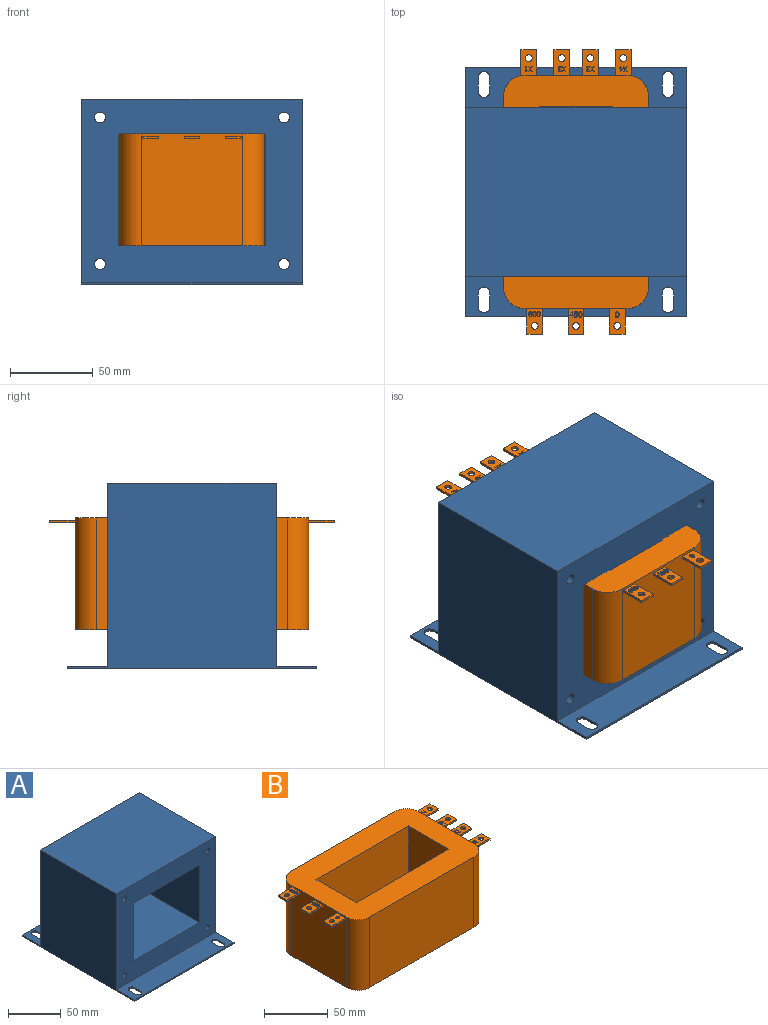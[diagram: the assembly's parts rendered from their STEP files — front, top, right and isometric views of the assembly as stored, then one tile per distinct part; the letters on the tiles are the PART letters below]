
ASSEMBLY  parts=2 mates=1
PART A: 34 faces, bbox 133.5x151x112.5 mm
  f0: plane 133.5x111mm, normal (0,-1,0), area 8744.3mm2, adj f2,f4,f22,f25,f26,f27,f28,f29
  f1: plane 133.5x111mm, normal (0,1,0), area 8744.3mm2, adj f4,f22,f23,f25,f26,f27,f28,f29
  f2: plane 133.5x24.35mm, normal (0,0,1), area 3052.5mm2, adj f0,f3,f4,f9,f10,f11,f12,f13
  f3: plane 133.5x1.5mm, normal (0,-1,0), area 200.2mm2, adj f2,f4,f22,f24
  f4: plane 151x112.5mm, normal (1,0,0), area 11581.8mm2, adj f0,f1,f2,f3,f5,f23,f24,f25
  f5: plane 133.5x1.5mm, normal (0,1,0), area 200.2mm2, adj f4,f22,f23,f24
  f6: cylinder r=3.54mm len=7.09mm, axis (0,0,-1), area 16.7mm2, adj f7,f18,f23,f24
  f7: plane 8.41x1.5mm, normal (-1,0,0), area 12.6mm2, adj f6,f8,f23,f24
  f8: cylinder r=3.54mm len=7.09mm, axis (0,0,-1), area 16.7mm2, adj f7,f18,f23,f24
  f9: plane 8.41x1.5mm, normal (-1,0,0), area 12.6mm2, adj f2,f10,f19,f24
  f10: cylinder r=3.54mm len=7.09mm, axis (0,0,-1), area 16.7mm2, adj f2,f9,f11,f24
  f11: plane 8.41x1.5mm, normal (1,0,0), area 12.6mm2, adj f2,f10,f19,f24
  f12: plane 8.41x1.5mm, normal (-1,0,0), area 12.6mm2, adj f2,f13,f20,f24
  f13: cylinder r=3.54mm len=7.09mm, axis (0,0,-1), area 16.7mm2, adj f2,f12,f14,f24
  f14: plane 8.41x1.5mm, normal (1,0,0), area 12.6mm2, adj f2,f13,f20,f24
  f15: plane 8.41x1.5mm, normal (1,0,0), area 12.6mm2, adj f16,f21,f23,f24
  f16: cylinder r=3.54mm len=7.09mm, axis (0,0,-1), area 16.7mm2, adj f15,f17,f23,f24
  f17: plane 8.41x1.5mm, normal (-1,0,0), area 12.6mm2, adj f16,f21,f23,f24
  f18: plane 8.41x1.5mm, normal (1,0,0), area 12.6mm2, adj f6,f8,f23,f24
  f19: cylinder r=3.54mm len=7.09mm, axis (0,0,-1), area 16.7mm2, adj f2,f9,f11,f24
  f20: cylinder r=3.54mm len=7.09mm, axis (0,0,-1), area 16.7mm2, adj f2,f12,f14,f24
  f21: cylinder r=3.54mm len=7.09mm, axis (0,0,-1), area 16.7mm2, adj f15,f17,f23,f24
  f22: plane 151x112.5mm, normal (-1,0,0), area 11581.8mm2, adj f0,f1,f2,f3,f5,f23,f24,f25
  f23: plane 133.5x24.35mm, normal (0,0,1), area 3052.5mm2, adj f1,f4,f5,f6,f7,f8,f15,f16
  f24: plane 151x133.5mm, normal (0,0,-1), area 19762.1mm2, adj f3,f4,f5,f6,f7,f8,f9,f10
  f25: plane 133.5x102.3mm, normal (0,0,1), area 13657mm2, adj f0,f1,f4,f22
  f26: plane 102.3x88.75mm, normal (0,0,1), area 9079.1mm2, adj f0,f1,f27,f29
  f27: plane 102.3x66.9mm, normal (-1,0,0), area 6843.9mm2, adj f0,f1,f26,f28
  f28: plane 102.3x88.75mm, normal (0,0,-1), area 9079.1mm2, adj f0,f1,f27,f29
  f29: plane 102.3x66.9mm, normal (1,0,0), area 6843.9mm2, adj f0,f1,f26,f28
  f30: cylinder r=3.3mm len=102.3mm, axis (0,-1,0), area 2121.1mm2, adj f0,f1
  f31: cylinder r=3.3mm len=102.3mm, axis (0,-1,0), area 2121.1mm2, adj f0,f1
  f32: cylinder r=3.3mm len=102.3mm, axis (0,-1,0), area 2121.1mm2, adj f0,f1
  f33: cylinder r=3.3mm len=102.3mm, axis (0,-1,0), area 2121.1mm2, adj f0,f1
PART B: 341 faces, bbox 172.3x87.8x67.6 mm
  f0: plane 15.5x9.5mm, normal (0,0,1), area 117.8mm2, adj f13,f36,f37,f38,f49,f271,f272,f273
  f1: plane 15.5x9.5mm, normal (0,0,1), area 127.1mm2, adj f13,f39,f41,f42,f48,f256,f257,f258
  f2: plane 15.5x9.5mm, normal (0,0,1), area 118.8mm2, adj f13,f43,f45,f46,f47,f196,f197,f198
  f3: plane 15.3x9.5mm, normal (0,0,1), area 127.8mm2, adj f9,f17,f19,f20,f53,f154,f155,f156
  f4: plane 15.3x9.5mm, normal (0,0,1), area 127mm2, adj f9,f21,f22,f24,f25,f52,f123,f124
  f5: plane 15.3x9.5mm, normal (0,0,1), area 128.6mm2, adj f9,f27,f28,f29,f30,f51,f100,f101
  f6: plane 15.3x9.5mm, normal (0,0,1), area 127.7mm2, adj f9,f31,f32,f34,f50,f58,f59,f60
  f7: plane 141.5x87.75mm, normal (0,0,1), area 7675.7mm2, adj f9,f10,f11,f12,f13,f14,f15,f16
  f8: plane 141.5x87.75mm, normal (0,0,-1), area 7675.7mm2, adj f9,f10,f11,f12,f13,f14,f15,f16
  f9: plane 67.6x61.75mm, normal (1,0,0), area 4124.8mm2, adj f3,f4,f5,f6,f7,f8,f10,f16
  f10: cylinder r=13mm len=67.6mm, axis (0,0,-1), area 1380.4mm2, adj f7,f8,f9,f11,f30
  f11: plane 115.5x67.6mm, normal (0,1,0), area 7807.8mm2, adj f7,f8,f10,f12
  f12: cylinder r=13mm len=67.6mm, axis (0,0,-1), area 1380.4mm2, adj f7,f8,f11,f13
  f13: plane 67.6x61.75mm, normal (-1,0,0), area 4131.6mm2, adj f0,f1,f2,f7,f8,f12,f14,f35
  f14: cylinder r=13mm len=67.6mm, axis (0,0,-1), area 1380.4mm2, adj f7,f8,f13,f15
  f15: plane 115.5x67.6mm, normal (0,-1,0), area 7807.8mm2, adj f7,f8,f14,f16
  f16: cylinder r=13mm len=67.6mm, axis (0,0,-1), area 1380.4mm2, adj f7,f8,f9,f15,f21
  f17: plane 15.3x1.5mm, normal (0,-1,0), area 23mm2, adj f3,f9,f18,f20
  f18: plane 15.3x9.5mm, normal (0,0,-1), area 132.1mm2, adj f9,f17,f19,f20,f53
  f19: plane 15.3x1.5mm, normal (0,1,0), area 23mm2, adj f3,f9,f18,f20
  f20: plane 9.5x1.5mm, normal (1,0,0), area 14.3mm2, adj f3,f17,f18,f19
  f21: plane 2.5x1.5mm, normal (-1,0,0), area 3.8mm2, adj f4,f16,f22,f23
  f22: plane 15.3x1.5mm, normal (0,-1,0), area 23mm2, adj f4,f21,f23,f25
  f23: plane 15.3x9.5mm, normal (0,0,-1), area 132.1mm2, adj f9,f21,f22,f24,f25,f52
  f24: plane 15.3x1.5mm, normal (0,1,0), area 23mm2, adj f4,f9,f23,f25
  f25: plane 9.5x1.5mm, normal (1,0,0), area 14.3mm2, adj f4,f22,f23,f24
  f26: plane 15.3x9.5mm, normal (0,0,-1), area 132.1mm2, adj f9,f27,f28,f29,f30,f51
  f27: plane 15.3x1.5mm, normal (0,1,0), area 23mm2, adj f5,f26,f29,f30
  f28: plane 15.3x1.5mm, normal (0,-1,0), area 23mm2, adj f5,f9,f26,f29
  f29: plane 9.5x1.5mm, normal (1,0,0), area 14.3mm2, adj f5,f26,f27,f28
  f30: plane 2.5x1.5mm, normal (-1,0,0), area 3.8mm2, adj f5,f10,f26,f27
  f31: plane 15.3x1.5mm, normal (0,1,0), area 23mm2, adj f6,f9,f33,f34
  f32: plane 15.3x1.5mm, normal (0,-1,0), area 23mm2, adj f6,f9,f33,f34
  f33: plane 15.3x9.5mm, normal (0,0,-1), area 132.1mm2, adj f9,f31,f32,f34,f50
  f34: plane 9.5x1.5mm, normal (1,0,0), area 14.3mm2, adj f6,f31,f32,f33
  f35: plane 15.5x9.5mm, normal (0,0,-1), area 134mm2, adj f13,f36,f37,f38,f49
  f36: plane 15.5x1.5mm, normal (0,-1,0), area 23.3mm2, adj f0,f13,f35,f38
  f37: plane 15.5x1.5mm, normal (0,1,0), area 23.3mm2, adj f0,f13,f35,f38
  f38: plane 9.5x1.5mm, normal (-1,0,0), area 14.3mm2, adj f0,f35,f36,f37
  f39: plane 15.5x1.5mm, normal (0,1,0), area 23.3mm2, adj f1,f13,f40,f42
  f40: plane 15.5x9.5mm, normal (0,0,-1), area 134mm2, adj f13,f39,f41,f42,f48
  f41: plane 15.5x1.5mm, normal (0,-1,0), area 23.3mm2, adj f1,f13,f40,f42
  f42: plane 9.5x1.5mm, normal (-1,0,0), area 14.3mm2, adj f1,f39,f40,f41
  f43: plane 15.5x1.5mm, normal (0,1,0), area 23.3mm2, adj f2,f13,f44,f46
  f44: plane 15.5x9.5mm, normal (0,0,-1), area 134mm2, adj f13,f43,f45,f46,f47
  f45: plane 15.5x1.5mm, normal (0,-1,0), area 23.3mm2, adj f2,f13,f44,f46
  f46: plane 9.5x1.5mm, normal (-1,0,0), area 14.3mm2, adj f2,f43,f44,f45
  f47: cylinder r=2.05mm len=4.1mm, axis (0,0,1), area 19.3mm2, adj f2,f44
  f48: cylinder r=2.05mm len=4.1mm, axis (0,0,1), area 19.3mm2, adj f1,f40
  f49: cylinder r=2.05mm len=4.1mm, axis (0,0,1), area 19.3mm2, adj f0,f35
  f50: cylinder r=2.05mm len=4.1mm, axis (0,0,1), area 19.3mm2, adj f6,f33
  f51: cylinder r=2.05mm len=4.1mm, axis (0,0,1), area 19.3mm2, adj f5,f26
  f52: cylinder r=2.05mm len=4.1mm, axis (0,0,1), area 19.3mm2, adj f4,f23
  f53: cylinder r=2.05mm len=4.1mm, axis (0,0,1), area 19.3mm2, adj f3,f18
  f54: plane 103x67.6mm, normal (0,1,0), area 6962.8mm2, adj f7,f8,f55,f57
  f55: plane 67.6x44.62mm, normal (-1,0,0), area 3016.3mm2, adj f7,f8,f54,f56
  f56: plane 103x67.6mm, normal (0,-1,0), area 6962.8mm2, adj f7,f8,f55,f57
  f57: plane 67.6x44.62mm, normal (1,0,0), area 3016.3mm2, adj f7,f8,f54,f56
  f58: extruded ~0.48x0.2mm, area 0.1mm2, adj f6,f59,f85,f86
  f59: extruded ~0.57x0.25mm, area 0.1mm2, adj f6,f58,f60,f86
  f60: extruded ~0.7x0.21mm, area 0.1mm2, adj f6,f59,f61,f86
  f61: extruded ~0.52x0.2mm, area 0.1mm2, adj f6,f60,f62,f86
  f62: extruded ~0.44x0.24mm, area 0.1mm2, adj f6,f61,f63,f86
  f63: plane 0.24x0.2mm, normal (-0.6,0.8,0), area 0.1mm2, adj f6,f62,f64,f86
  f64: extruded ~0.41x0.2mm, area 0.1mm2, adj f6,f63,f65,f86
  f65: extruded ~0.38x0.2mm, area 0.1mm2, adj f6,f64,f66,f86
  f66: extruded ~0.42x0.2mm, area 0.1mm2, adj f6,f65,f67,f86
  f67: extruded ~0.36x0.2mm, area 0.1mm2, adj f6,f66,f68,f86
  f68: extruded ~0.44x0.21mm, area 0.1mm2, adj f6,f67,f69,f86
  f69: extruded ~0.57x0.2mm, area 0.1mm2, adj f6,f68,f70,f86
  f70: plane 0.31x0.2mm, normal (1,0,0), area 0.1mm2, adj f6,f69,f71,f86
  f71: plane 0.3x0.2mm, normal (0,1,0), area 0.1mm2, adj f6,f70,f72,f86
  f72: plane 0.3x0.2mm, normal (-1,0,0), area 0.1mm2, adj f6,f71,f73,f86
  f73: extruded ~0.88x0.56mm, area 0.2mm2, adj f6,f72,f74,f86
  f74: extruded ~0.8x0.63mm, area 0.2mm2, adj f6,f73,f75,f86
  f75: extruded ~0.43x0.2mm, area 0.1mm2, adj f6,f74,f76,f86
  f76: extruded ~0.43x0.2mm, area 0.1mm2, adj f6,f75,f77,f86
  f77: plane 0.33x0.2mm, normal (0,1,0), area 0.1mm2, adj f6,f76,f78,f86
  f78: extruded ~0.4x0.2mm, area 0.1mm2, adj f6,f77,f79,f86
  f79: extruded ~0.45x0.2mm, area 0.1mm2, adj f6,f78,f80,f86
  f80: extruded ~0.87x0.24mm, area 0.2mm2, adj f6,f79,f81,f86
  f81: extruded ~0.68x0.31mm, area 0.2mm2, adj f6,f80,f82,f86
  f82: extruded ~0.5x0.2mm, area 0.1mm2, adj f6,f81,f83,f86
  f83: extruded ~0.55x0.24mm, area 0.1mm2, adj f6,f82,f84,f86
  f84: plane 0.2x0.02mm, normal (0,-1,0), area 0mm2, adj f6,f83,f85,f86
  f85: extruded ~0.47x0.25mm, area 0.1mm2, adj f6,f58,f84,f86
  f86: plane 3.18x2.02mm, normal (0,0,1), area 2.2mm2, adj f58,f59,f60,f61,f62,f63,f64,f65
  f87: plane 0.41x0.2mm, normal (-1,0,0), area 0.1mm2, adj f6,f88,f98,f99
  f88: plane 1.63x1.03mm, normal (0.54,-0.84,0), area 0.4mm2, adj f6,f87,f89,f99
  f89: plane 1.46x0.96mm, normal (-0.55,-0.84,0), area 0.3mm2, adj f6,f88,f90,f99
  f90: plane 0.38x0.2mm, normal (1,0,0), area 0.1mm2, adj f6,f89,f91,f99
  f91: plane 1.22x0.77mm, normal (0.53,0.85,0), area 0.3mm2, adj f6,f90,f92,f99
  f92: plane 1.22x0.77mm, normal (0.53,-0.85,0), area 0.3mm2, adj f6,f91,f93,f99
  f93: plane 0.4x0.2mm, normal (1,0,0), area 0.1mm2, adj f6,f92,f94,f99
  f94: plane 1.48x0.96mm, normal (-0.54,0.84,0), area 0.4mm2, adj f6,f93,f95,f99
  f95: plane 1.62x1.03mm, normal (0.54,0.84,0), area 0.4mm2, adj f6,f94,f96,f99
  f96: plane 0.38x0.2mm, normal (-1,0,0), area 0.1mm2, adj f6,f95,f97,f99
  f97: plane 1.36x0.85mm, normal (-0.53,-0.85,0), area 0.3mm2, adj f6,f96,f98,f99
  f98: plane 1.36x0.83mm, normal (-0.52,0.85,0), area 0.3mm2, adj f6,f87,f97,f99
  f99: plane 3.09x2.46mm, normal (0,0,1), area 2.2mm2, adj f87,f88,f89,f90,f91,f92,f93,f94
  f100: plane 0.34x0.2mm, normal (-1,0,0), area 0.1mm2, adj f5,f101,f108,f109
  f101: plane 3.09x0.2mm, normal (0,-1,0), area 0.6mm2, adj f5,f100,f102,f109
  f102: plane 0.3x0.2mm, normal (1,0,0), area 0.1mm2, adj f5,f101,f103,f109
  f103: plane 0.82x0.63mm, normal (0.79,0.61,0), area 0.2mm2, adj f5,f102,f104,f109
  f104: plane 0.24x0.2mm, normal (-0.61,0.79,0), area 0.1mm2, adj f5,f103,f105,f109
  f105: extruded ~0.5x0.41mm, area 0.1mm2, adj f5,f104,f106,f109
  f106: extruded ~0.2x0.1mm, area 0mm2, adj f5,f105,f107,f109
  f107: extruded ~0.52x0.2mm, area 0.1mm2, adj f5,f106,f108,f109
  f108: plane 2.2x0.2mm, normal (0,1,0), area 0.4mm2, adj f5,f100,f107,f109
  f109: plane 3.09x1.11mm, normal (0,0,1), area 1.3mm2, adj f100,f101,f102,f103,f104,f105,f106,f107
  f110: plane 0.41x0.2mm, normal (-1,0,0), area 0.1mm2, adj f5,f111,f121,f122
  f111: plane 1.63x1.03mm, normal (0.54,-0.84,0), area 0.4mm2, adj f5,f110,f112,f122
  f112: plane 1.46x0.96mm, normal (-0.55,-0.84,0), area 0.3mm2, adj f5,f111,f113,f122
  f113: plane 0.38x0.2mm, normal (1,0,0), area 0.1mm2, adj f5,f112,f114,f122
  f114: plane 1.22x0.77mm, normal (0.53,0.85,0), area 0.3mm2, adj f5,f113,f115,f122
  f115: plane 1.22x0.77mm, normal (0.53,-0.85,0), area 0.3mm2, adj f5,f114,f116,f122
  f116: plane 0.4x0.2mm, normal (1,0,0), area 0.1mm2, adj f5,f115,f117,f122
  f117: plane 1.48x0.96mm, normal (-0.54,0.84,0), area 0.4mm2, adj f5,f116,f118,f122
  f118: plane 1.62x1.03mm, normal (0.54,0.84,0), area 0.4mm2, adj f5,f117,f119,f122
  f119: plane 0.38x0.2mm, normal (-1,0,0), area 0.1mm2, adj f5,f118,f120,f122
  f120: plane 1.36x0.85mm, normal (-0.53,-0.85,0), area 0.3mm2, adj f5,f119,f121,f122
  f121: plane 1.36x0.83mm, normal (-0.52,0.85,0), area 0.3mm2, adj f5,f110,f120,f122
  f122: plane 3.09x2.46mm, normal (0,0,1), area 2.2mm2, adj f110,f111,f112,f113,f114,f115,f116,f117
  f123: plane 0.39x0.2mm, normal (-1,0,0), area 0.1mm2, adj f4,f124,f134,f135
  f124: plane 1.57x1mm, normal (0.54,-0.84,0), area 0.4mm2, adj f4,f123,f125,f135
  f125: plane 1.42x0.93mm, normal (-0.55,-0.84,0), area 0.3mm2, adj f4,f124,f126,f135
  f126: plane 0.37x0.2mm, normal (1,0,0), area 0.1mm2, adj f4,f125,f127,f135
  f127: plane 1.18x0.75mm, normal (0.53,0.85,0), area 0.3mm2, adj f4,f126,f128,f135
  f128: plane 1.18x0.74mm, normal (0.53,-0.85,0), area 0.3mm2, adj f4,f127,f129,f135
  f129: plane 0.39x0.2mm, normal (1,0,0), area 0.1mm2, adj f4,f128,f130,f135
  f130: plane 1.43x0.93mm, normal (-0.54,0.84,0), area 0.3mm2, adj f4,f129,f131,f135
  f131: plane 1.56x0.99mm, normal (0.54,0.84,0), area 0.4mm2, adj f4,f130,f132,f135
  f132: plane 0.37x0.2mm, normal (-1,0,0), area 0.1mm2, adj f4,f131,f133,f135
  f133: plane 1.31x0.82mm, normal (-0.53,-0.85,0), area 0.3mm2, adj f4,f132,f134,f135
  f134: plane 1.31x0.8mm, normal (-0.52,0.85,0), area 0.3mm2, adj f4,f123,f133,f135
  f135: plane 2.99x2.39mm, normal (0,0,1), area 2.1mm2, adj f123,f124,f125,f126,f127,f128,f129,f130
  f136: plane 0.99x0.2mm, normal (0,1,0), area 0.2mm2, adj f137,f152,f153,f188
  f137: plane 1.11x0.2mm, normal (1,0,0), area 0.2mm2, adj f136,f138,f153,f188
  f138: plane 1.33x0.93mm, normal (-0.58,-0.82,0), area 0.3mm2, adj f137,f139,f153,f188
  f139: extruded ~0.33x0.2mm, area 0.1mm2, adj f138,f140,f153,f188
  f140: plane 0.2x0.02mm, normal (-1,0,0), area 0mm2, adj f139,f152,f153,f188
  f141: plane 0.44x0.2mm, normal (-1,0,0), area 0.1mm2, adj f4,f142,f151,f153
  f142: plane 0.31x0.2mm, normal (0,-1,0), area 0.1mm2, adj f4,f141,f143,f153
  f143: plane 0.44x0.2mm, normal (1,0,0), area 0.1mm2, adj f4,f142,f144,f153
  f144: plane 2.01x0.2mm, normal (0,-1,0), area 0.4mm2, adj f4,f143,f145,f153
  f145: plane 0.36x0.2mm, normal (1,0,0), area 0.1mm2, adj f4,f144,f146,f153
  f146: plane 2.02x1.42mm, normal (0.57,0.82,0), area 0.5mm2, adj f4,f145,f147,f153
  f147: plane 0.3x0.2mm, normal (0,1,0), area 0.1mm2, adj f4,f146,f148,f153
  f148: plane 1.45x0.2mm, normal (-1,0,0), area 0.3mm2, adj f4,f147,f149,f153
  f149: plane 0.69x0.2mm, normal (0,1,0), area 0.1mm2, adj f4,f148,f150,f153
  f150: plane 0.33x0.2mm, normal (-1,0,0), area 0.1mm2, adj f4,f149,f151,f153
  f151: plane 0.69x0.2mm, normal (0,-1,0), area 0.1mm2, adj f4,f141,f150,f153
  f152: extruded ~0.66x0.2mm, area 0.1mm2, adj f136,f140,f153,f188
  f153: plane 3.01x2.22mm, normal (0,0,1), area 2.2mm2, adj f136,f137,f138,f139,f140,f141,f142,f143
  f154: plane 0.41x0.2mm, normal (-1,0,0), area 0.1mm2, adj f3,f155,f165,f166
  f155: plane 1.62x1.03mm, normal (0.54,-0.84,0), area 0.4mm2, adj f3,f154,f156,f166
  f156: plane 1.46x0.95mm, normal (-0.55,-0.84,0), area 0.3mm2, adj f3,f155,f157,f166
  f157: plane 0.38x0.2mm, normal (1,0,0), area 0.1mm2, adj f3,f156,f158,f166
  f158: plane 1.22x0.77mm, normal (0.53,0.85,0), area 0.3mm2, adj f3,f157,f159,f166
  f159: plane 1.22x0.76mm, normal (0.53,-0.85,0), area 0.3mm2, adj f3,f158,f160,f166
  f160: plane 0.4x0.2mm, normal (1,0,0), area 0.1mm2, adj f3,f159,f161,f166
  f161: plane 1.47x0.95mm, normal (-0.54,0.84,0), area 0.4mm2, adj f3,f160,f162,f166
  f162: plane 1.61x1.02mm, normal (0.54,0.84,0), area 0.4mm2, adj f3,f161,f163,f166
  f163: plane 0.38x0.2mm, normal (-1,0,0), area 0.1mm2, adj f3,f162,f164,f166
  f164: plane 1.35x0.84mm, normal (-0.53,-0.85,0), area 0.3mm2, adj f3,f163,f165,f166
  f165: plane 1.35x0.83mm, normal (-0.52,0.85,0), area 0.3mm2, adj f3,f154,f164,f166
  f166: plane 3.08x2.45mm, normal (0,0,1), area 2.2mm2, adj f154,f155,f156,f157,f158,f159,f160,f161
  f167: plane 2.02x0.2mm, normal (-1,0,0), area 0.4mm2, adj f3,f168,f186,f187
  f168: plane 0.32x0.2mm, normal (0,-1,0), area 0.1mm2, adj f3,f167,f169,f187
  f169: plane 1.58x0.2mm, normal (1,0,0), area 0.3mm2, adj f3,f168,f170,f187
  f170: plane 0.2x0.02mm, normal (0,-1,0), area 0mm2, adj f3,f169,f171,f187
  f171: plane 0.67x0.66mm, normal (-0.71,-0.7,0), area 0.2mm2, adj f3,f170,f172,f187
  f172: extruded ~0.72x0.61mm, area 0.2mm2, adj f3,f171,f173,f187
  f173: extruded ~0.58x0.2mm, area 0.1mm2, adj f3,f172,f174,f187
  f174: extruded ~0.6x0.25mm, area 0.1mm2, adj f3,f173,f175,f187
  f175: extruded ~0.68x0.22mm, area 0.1mm2, adj f3,f174,f176,f187
  f176: extruded ~0.93x0.35mm, area 0.2mm2, adj f3,f175,f177,f187
  f177: plane 0.24x0.2mm, normal (-0.61,0.79,0), area 0.1mm2, adj f3,f176,f178,f187
  f178: extruded ~0.38x0.23mm, area 0.1mm2, adj f3,f177,f179,f187
  f179: extruded ~0.36x0.2mm, area 0.1mm2, adj f3,f178,f180,f187
  f180: extruded ~0.42x0.2mm, area 0.1mm2, adj f3,f179,f181,f187
  f181: extruded ~0.39x0.2mm, area 0.1mm2, adj f3,f180,f182,f187
  f182: extruded ~0.33x0.2mm, area 0.1mm2, adj f3,f181,f183,f187
  f183: extruded ~0.31x0.2mm, area 0.1mm2, adj f3,f182,f184,f187
  f184: extruded ~0.54x0.49mm, area 0.1mm2, adj f3,f183,f185,f187
  f185: plane 0.81x0.81mm, normal (0.71,0.71,0), area 0.2mm2, adj f3,f184,f186,f187
  f186: plane 0.3x0.2mm, normal (0,1,0), area 0.1mm2, adj f3,f167,f185,f187
  f187: plane 3.12x2.02mm, normal (0,0,1), area 2.1mm2, adj f167,f168,f169,f170,f171,f172,f173,f174
  f188: plane 1.65x1.14mm, normal (0,0,1), area 0.9mm2, adj f136,f137,f138,f139,f140,f152
  f189: extruded ~1x0.2mm, area 0.2mm2, adj f190,f204,f205,f334
  f190: extruded ~1x0.2mm, area 0.2mm2, adj f189,f191,f205,f334
  f191: extruded ~0.51x0.31mm, area 0.1mm2, adj f190,f192,f205,f334
  f192: extruded ~0.52x0.32mm, area 0.1mm2, adj f191,f193,f205,f334
  f193: extruded ~0.99x0.2mm, area 0.2mm2, adj f192,f194,f205,f334
  f194: extruded ~1x0.2mm, area 0.2mm2, adj f193,f195,f205,f334
  f195: extruded ~0.52x0.32mm, area 0.1mm2, adj f194,f204,f205,f334
  f196: extruded ~1.22x0.26mm, area 0.3mm2, adj f2,f197,f203,f205
  f197: extruded ~1.2x0.27mm, area 0.2mm2, adj f2,f196,f198,f205
  f198: extruded ~0.78x0.42mm, area 0.2mm2, adj f2,f197,f199,f205
  f199: extruded ~0.78x0.4mm, area 0.2mm2, adj f2,f198,f200,f205
  f200: extruded ~1.22x0.26mm, area 0.3mm2, adj f2,f199,f201,f205
  f201: extruded ~1.21x0.26mm, area 0.3mm2, adj f2,f200,f202,f205
  f202: extruded ~0.77x0.41mm, area 0.2mm2, adj f2,f201,f203,f205
  f203: extruded ~0.79x0.4mm, area 0.2mm2, adj f2,f196,f202,f205
  f204: extruded ~0.51x0.31mm, area 0.1mm2, adj f189,f195,f205,f334
  f205: plane 3.24x2.08mm, normal (0,0,1), area 2.6mm2, adj f189,f190,f191,f192,f193,f194,f195,f196
  f206: extruded ~1x0.2mm, area 0.2mm2, adj f207,f221,f222,f335
  f207: extruded ~1x0.2mm, area 0.2mm2, adj f206,f208,f222,f335
  f208: extruded ~0.51x0.31mm, area 0.1mm2, adj f207,f209,f222,f335
  f209: extruded ~0.52x0.32mm, area 0.1mm2, adj f208,f210,f222,f335
  f210: extruded ~0.99x0.2mm, area 0.2mm2, adj f209,f211,f222,f335
  f211: extruded ~1x0.2mm, area 0.2mm2, adj f210,f212,f222,f335
  f212: extruded ~0.52x0.32mm, area 0.1mm2, adj f211,f221,f222,f335
  f213: extruded ~1.22x0.26mm, area 0.3mm2, adj f2,f214,f220,f222
  f214: extruded ~1.2x0.27mm, area 0.2mm2, adj f2,f213,f215,f222
  f215: extruded ~0.78x0.42mm, area 0.2mm2, adj f2,f214,f216,f222
  f216: extruded ~0.78x0.4mm, area 0.2mm2, adj f2,f215,f217,f222
  f217: extruded ~1.22x0.26mm, area 0.3mm2, adj f2,f216,f218,f222
  f218: extruded ~1.21x0.26mm, area 0.3mm2, adj f2,f217,f219,f222
  f219: extruded ~0.77x0.41mm, area 0.2mm2, adj f2,f218,f220,f222
  f220: extruded ~0.79x0.4mm, area 0.2mm2, adj f2,f213,f219,f222
  f221: extruded ~0.51x0.31mm, area 0.1mm2, adj f206,f212,f222,f335
  f222: plane 3.24x2.08mm, normal (0,0,1), area 2.6mm2, adj f206,f207,f208,f209,f210,f211,f212,f213
  f223: extruded ~0.47x0.2mm, area 0.1mm2, adj f224,f247,f248,f336
  f224: extruded ~0.36x0.2mm, area 0.1mm2, adj f223,f225,f248,f336
  f225: extruded ~0.3x0.24mm, area 0.1mm2, adj f224,f226,f248,f336
  f226: extruded ~0.41x0.2mm, area 0.1mm2, adj f225,f227,f248,f336
  f227: extruded ~0.29x0.2mm, area 0.1mm2, adj f226,f228,f248,f336
  f228: extruded ~0.26x0.22mm, area 0.1mm2, adj f227,f229,f248,f336
  f229: extruded ~0.36x0.2mm, area 0.1mm2, adj f228,f230,f248,f336
  f230: extruded ~0.47x0.2mm, area 0.1mm2, adj f229,f231,f248,f336
  f231: extruded ~0.49x0.2mm, area 0.1mm2, adj f230,f247,f248,f336
  f232: extruded ~1.39x0.36mm, area 0.3mm2, adj f2,f233,f246,f248
  f233: extruded ~1.02x0.29mm, area 0.2mm2, adj f2,f232,f234,f248
  f234: extruded ~0.77x0.37mm, area 0.2mm2, adj f2,f233,f235,f248
  f235: extruded ~0.72x0.28mm, area 0.2mm2, adj f2,f234,f236,f248
  f236: extruded ~0.77x0.27mm, area 0.2mm2, adj f2,f235,f237,f248
  f237: extruded ~0.69x0.24mm, area 0.2mm2, adj f2,f236,f238,f248
  f238: extruded ~0.67x0.26mm, area 0.1mm2, adj f2,f237,f239,f248
  f239: extruded ~0.75x0.37mm, area 0.2mm2, adj f2,f238,f240,f248
  f240: plane 0.2x0.03mm, normal (-1,0,0), area 0mm2, adj f2,f239,f241,f248
  f241: extruded ~0.99x0.29mm, area 0.2mm2, adj f2,f240,f242,f248
  f242: extruded ~0.77x0.32mm, area 0.2mm2, adj f2,f241,f243,f248
  f243: extruded ~0.38x0.2mm, area 0.1mm2, adj f2,f242,f244,f248
  f244: plane 0.31x0.2mm, normal (0,1,0), area 0.1mm2, adj f2,f243,f245,f248
  f245: extruded ~0.38x0.2mm, area 0.1mm2, adj f2,f244,f246,f248
  f246: extruded ~1.07x0.46mm, area 0.2mm2, adj f2,f232,f245,f248
  f247: extruded ~0.56x0.2mm, area 0.1mm2, adj f223,f231,f248,f336
  f248: plane 3.23x2.05mm, normal (0,0,1), area 2.6mm2, adj f223,f224,f225,f226,f227,f228,f229,f230
  f249: extruded ~1.11x0.2mm, area 0.2mm2, adj f250,f264,f265,f337
  f250: extruded ~1.11x0.2mm, area 0.2mm2, adj f249,f251,f265,f337
  f251: extruded ~0.57x0.35mm, area 0.1mm2, adj f250,f252,f265,f337
  f252: extruded ~0.58x0.35mm, area 0.1mm2, adj f251,f253,f265,f337
  f253: extruded ~1.11x0.2mm, area 0.2mm2, adj f252,f254,f265,f337
  f254: extruded ~1.11x0.2mm, area 0.2mm2, adj f253,f255,f265,f337
  f255: extruded ~0.58x0.35mm, area 0.1mm2, adj f254,f264,f265,f337
  f256: extruded ~1.36x0.29mm, area 0.3mm2, adj f1,f257,f263,f265
  f257: extruded ~1.34x0.3mm, area 0.3mm2, adj f1,f256,f258,f265
  f258: extruded ~0.87x0.46mm, area 0.2mm2, adj f1,f257,f259,f265
  f259: extruded ~0.87x0.44mm, area 0.2mm2, adj f1,f258,f260,f265
  f260: extruded ~1.36x0.29mm, area 0.3mm2, adj f1,f259,f261,f265
  f261: extruded ~1.35x0.3mm, area 0.3mm2, adj f1,f260,f262,f265
  f262: extruded ~0.86x0.46mm, area 0.2mm2, adj f1,f261,f263,f265
  f263: extruded ~0.88x0.45mm, area 0.2mm2, adj f1,f256,f262,f265
  f264: extruded ~0.57x0.35mm, area 0.1mm2, adj f249,f255,f265,f337
  f265: plane 3.61x2.32mm, normal (0,0,1), area 3.2mm2, adj f249,f250,f251,f252,f253,f254,f255,f256
  f266: plane 1.12x0.2mm, normal (0,-1,0), area 0.2mm2, adj f267,f282,f283,f338
  f267: plane 1.25x0.2mm, normal (-1,0,0), area 0.3mm2, adj f266,f268,f283,f338
  f268: plane 1.49x1.05mm, normal (0.58,0.82,0), area 0.4mm2, adj f267,f269,f283,f338
  f269: extruded ~0.37x0.21mm, area 0.1mm2, adj f268,f270,f283,f338
  f270: plane 0.2x0.02mm, normal (1,0,0), area 0mm2, adj f269,f282,f283,f338
  f271: plane 0.5x0.2mm, normal (1,0,0), area 0.1mm2, adj f0,f272,f281,f283
  f272: plane 0.35x0.2mm, normal (0,1,0), area 0.1mm2, adj f0,f271,f273,f283
  f273: plane 0.5x0.2mm, normal (-1,0,0), area 0.1mm2, adj f0,f272,f274,f283
  f274: plane 2.26x0.2mm, normal (0,1,0), area 0.5mm2, adj f0,f273,f275,f283
  f275: plane 0.4x0.2mm, normal (-1,0,0), area 0.1mm2, adj f0,f274,f276,f283
  f276: plane 2.28x1.6mm, normal (-0.57,-0.82,0), area 0.6mm2, adj f0,f275,f277,f283
  f277: plane 0.33x0.2mm, normal (0,-1,0), area 0.1mm2, adj f0,f276,f278,f283
  f278: plane 1.64x0.2mm, normal (1,0,0), area 0.3mm2, adj f0,f277,f279,f283
  f279: plane 0.77x0.2mm, normal (0,-1,0), area 0.2mm2, adj f0,f278,f280,f283
  f280: plane 0.37x0.2mm, normal (1,0,0), area 0.1mm2, adj f0,f279,f281,f283
  f281: plane 0.77x0.2mm, normal (0,1,0), area 0.2mm2, adj f0,f271,f280,f283
  f282: extruded ~0.74x0.2mm, area 0.1mm2, adj f266,f270,f283,f338
  f283: plane 3.38x2.5mm, normal (0,0,1), area 2.7mm2, adj f266,f267,f268,f269,f270,f271,f272,f273
  f284: extruded ~0.45x0.2mm, area 0.1mm2, adj f285,f314,f315,f339
  f285: extruded ~0.46x0.2mm, area 0.1mm2, adj f284,f286,f315,f339
  f286: extruded ~0.37x0.2mm, area 0.1mm2, adj f285,f287,f315,f339
  f287: extruded ~0.37x0.2mm, area 0.1mm2, adj f286,f288,f315,f339
  f288: extruded ~0.47x0.3mm, area 0.1mm2, adj f287,f289,f315,f339
  f289: extruded ~0.5x0.3mm, area 0.1mm2, adj f288,f290,f315,f339
  f290: extruded ~0.36x0.2mm, area 0.1mm2, adj f289,f314,f315,f339
  f291: extruded ~0.43x0.2mm, area 0.1mm2, adj f292,f312,f315,f316
  f292: extruded ~0.43x0.2mm, area 0.1mm2, adj f291,f293,f315,f316
  f293: extruded ~0.5x0.33mm, area 0.1mm2, adj f292,f294,f315,f316
  f294: extruded ~0.63x0.34mm, area 0.1mm2, adj f293,f295,f315,f316
  f295: extruded ~0.4x0.2mm, area 0.1mm2, adj f294,f296,f315,f316
  f296: extruded ~0.44x0.2mm, area 0.1mm2, adj f295,f297,f315,f316
  f297: extruded ~0.53x0.2mm, area 0.1mm2, adj f296,f312,f315,f316
  f298: extruded ~0.73x0.21mm, area 0.2mm2, adj f0,f299,f313,f315
  f299: extruded ~0.72x0.22mm, area 0.2mm2, adj f0,f298,f300,f315
  f300: extruded ~0.58x0.27mm, area 0.1mm2, adj f0,f299,f301,f315
  f301: extruded ~0.47x0.2mm, area 0.1mm2, adj f0,f300,f302,f315
  f302: extruded ~0.46x0.39mm, area 0.1mm2, adj f0,f301,f303,f315
  f303: extruded ~0.9x0.7mm, area 0.2mm2, adj f0,f302,f304,f315
  f304: extruded ~0.67x0.29mm, area 0.2mm2, adj f0,f303,f305,f315
  f305: extruded ~0.83x0.24mm, area 0.2mm2, adj f0,f304,f306,f315
  f306: extruded ~0.8x0.25mm, area 0.2mm2, adj f0,f305,f307,f315
  f307: extruded ~0.67x0.29mm, area 0.2mm2, adj f0,f306,f308,f315
  f308: extruded ~0.5x0.2mm, area 0.1mm2, adj f0,f307,f309,f315
  f309: extruded ~0.58x0.41mm, area 0.1mm2, adj f0,f308,f310,f315
  f310: extruded ~0.49x0.37mm, area 0.1mm2, adj f0,f309,f311,f315
  f311: extruded ~0.45x0.2mm, area 0.1mm2, adj f0,f310,f313,f315
  f312: extruded ~0.54x0.2mm, area 0.1mm2, adj f291,f297,f315,f316
  f313: extruded ~0.59x0.27mm, area 0.1mm2, adj f0,f298,f311,f315
  f314: extruded ~0.37x0.2mm, area 0.1mm2, adj f284,f290,f315,f339
  f315: plane 3.46x2.21mm, normal (0,0,1), area 3.3mm2, adj f284,f285,f286,f287,f288,f289,f290,f291
  f316: plane 1.46x1.34mm, normal (0,0,1), area 1.5mm2, adj f291,f292,f293,f294,f295,f296,f297,f312
  f317: extruded ~1.07x0.2mm, area 0.2mm2, adj f318,f332,f333,f340
  f318: extruded ~1.07x0.2mm, area 0.2mm2, adj f317,f319,f333,f340
  f319: extruded ~0.55x0.33mm, area 0.1mm2, adj f318,f320,f333,f340
  f320: extruded ~0.55x0.34mm, area 0.1mm2, adj f319,f321,f333,f340
  f321: extruded ~1.06x0.2mm, area 0.2mm2, adj f320,f322,f333,f340
  f322: extruded ~1.06x0.2mm, area 0.2mm2, adj f321,f323,f333,f340
  f323: extruded ~0.55x0.34mm, area 0.1mm2, adj f322,f332,f333,f340
  f324: extruded ~1.3x0.28mm, area 0.3mm2, adj f0,f325,f331,f333
  f325: extruded ~1.29x0.28mm, area 0.3mm2, adj f0,f324,f326,f333
  f326: extruded ~0.83x0.44mm, area 0.2mm2, adj f0,f325,f327,f333
  f327: extruded ~0.83x0.43mm, area 0.2mm2, adj f0,f326,f328,f333
  f328: extruded ~1.3x0.27mm, area 0.3mm2, adj f0,f327,f329,f333
  f329: extruded ~1.29x0.28mm, area 0.3mm2, adj f0,f328,f330,f333
  f330: extruded ~0.83x0.44mm, area 0.2mm2, adj f0,f329,f331,f333
  f331: extruded ~0.84x0.43mm, area 0.2mm2, adj f0,f324,f330,f333
  f332: extruded ~0.55x0.34mm, area 0.1mm2, adj f317,f323,f333,f340
  f333: plane 3.46x2.22mm, normal (0,0,1), area 3mm2, adj f317,f318,f319,f320,f321,f322,f323,f324
  f334: plane 2.62x1.35mm, normal (0,0,1), area 3mm2, adj f189,f190,f191,f192,f193,f194,f195,f204
  f335: plane 2.62x1.35mm, normal (0,0,1), area 3mm2, adj f206,f207,f208,f209,f210,f211,f212,f221
  f336: plane 1.42x1.33mm, normal (0,0,1), area 1.5mm2, adj f223,f224,f225,f226,f227,f228,f229,f230
  f337: plane 2.92x1.51mm, normal (0,0,1), area 3.7mm2, adj f249,f250,f251,f252,f253,f254,f255,f264
  f338: plane 1.86x1.28mm, normal (0,0,1), area 1.1mm2, adj f266,f267,f268,f269,f270,f282
  f339: plane 1.24x1.17mm, normal (0,0,1), area 1.1mm2, adj f284,f285,f286,f287,f288,f289,f290,f314
  f340: plane 2.8x1.45mm, normal (0,0,1), area 3.4mm2, adj f317,f318,f319,f320,f321,f322,f323,f332
PLACE A t=(-59.55,-0.79,-5.87)mm
PLACE B rot(axis=(0,0,1),90deg) t=(-59.55,-0.79,17.93)mm
MATE fastened B.f8 <-> A.f26  axis (0,0,-1) through (-59.55,-0.79,17.93)mm
